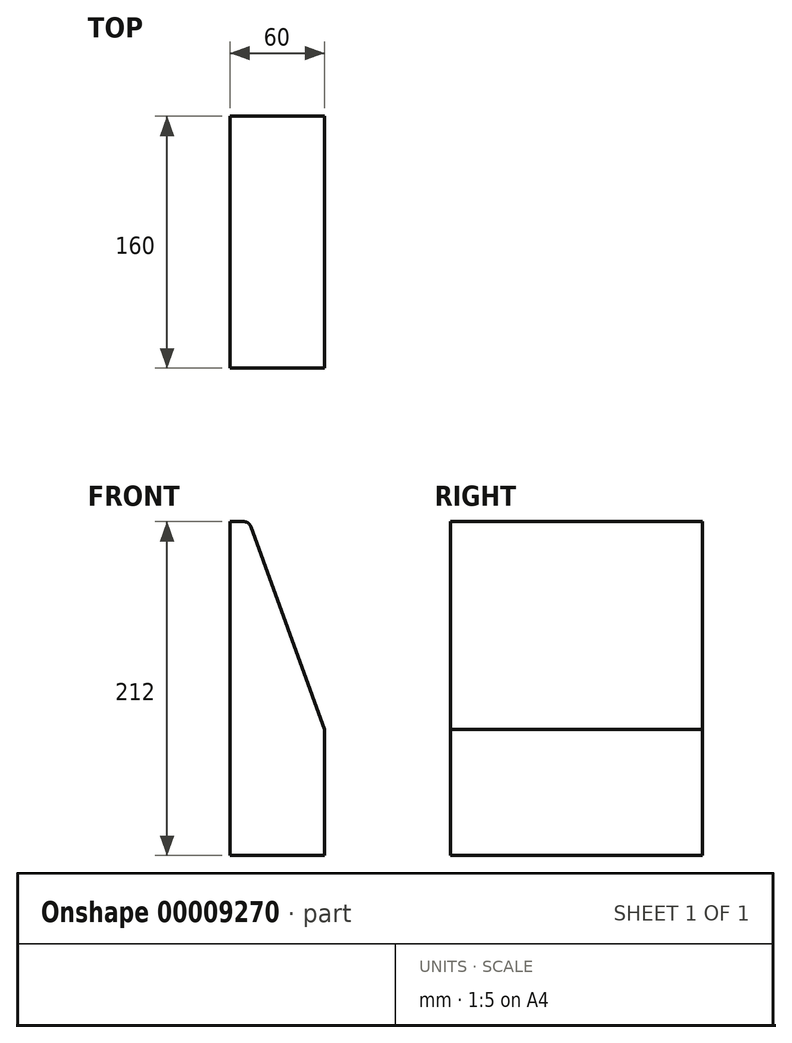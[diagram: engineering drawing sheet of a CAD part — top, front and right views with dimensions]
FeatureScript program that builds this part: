
annotation { "Feature Type Name" : "Feature", "Feature Type Description" : "" }
export const myFeature = defineFeature(function(context is Context, id is Id, definition is map)
    precondition{}
    {
        {
            var Q0;
            Q0=qCreatedBy(makeId("Front.planeOp"),FACE);
            var sketch = newSketch(context, id + "F0", { "sketchPlane" : qUnion([Q0])});
            skLineSegment(sketch, "E0", {"start": v(0, 0) * mm, "end": v(0, 80) * mm});
            skLineSegment(sketch, "E1", {"start": v(0, 80) * mm, "end": v(-48, 212) * mm});
            skLineSegment(sketch, "E2", {"start": v(-48, 212) * mm, "end": v(-60, 212) * mm});
            skLineSegment(sketch, "E3", {"start": v(-60, 212) * mm, "end": v(-60, 0) * mm});
            skLineSegment(sketch, "E4", {"start": v(-60, 0) * mm, "end": v(0, 0) * mm});
            skSolve(sketch);
        }
        {
            var Q0;
            Q0 = qSketchRegion(id + "F0", true);
            extrude(context, id + "F1", {"entities" : qUnion([Q0]), "oppositeDirection" : true, "depth" : 160 * mm});
        }
        {
            var Q0;
            Q0=makeQuery(id+"F1.opExtrude","SWEPT_EDGE",EDGE,{"disambiguationData":[OSD([sQuery(id+"F0.wireOp",EDGE,"E1"),sQuery(id+"F0.wireOp",EDGE,"E2")])]});
            fillet(context, id + "F2", {"entities" : qUnion([Q0]), "radius" : 5 * mm, "tangentPropagation" : true, "allowEdgeOverflow" : false});
        }
    });
